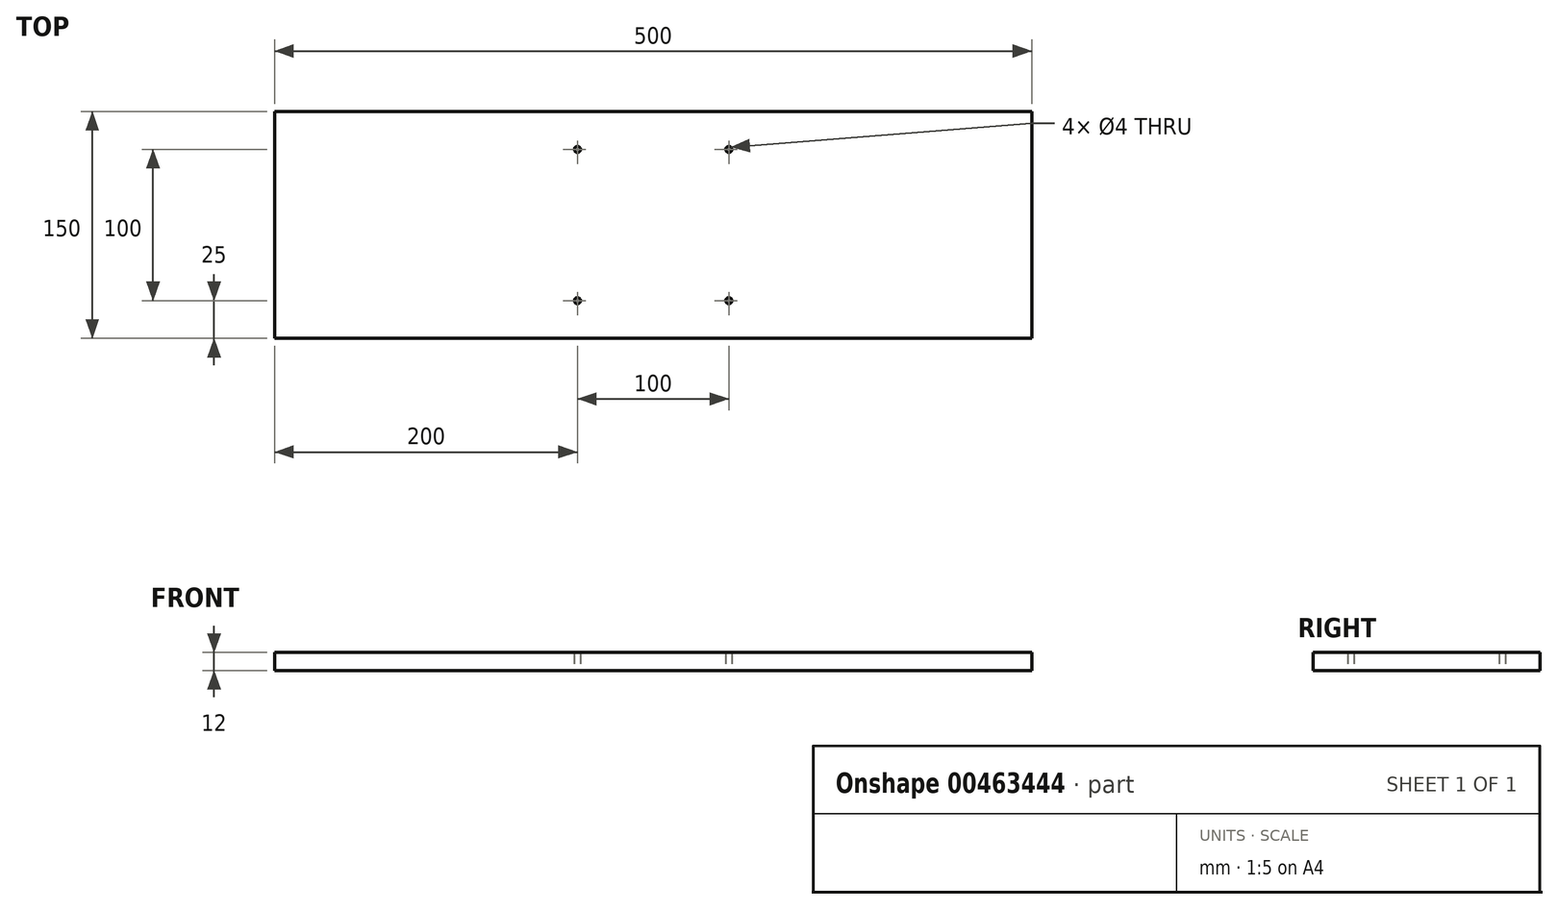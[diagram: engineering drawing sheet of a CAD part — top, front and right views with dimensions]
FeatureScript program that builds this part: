
annotation { "Feature Type Name" : "Feature", "Feature Type Description" : "" }
export const myFeature = defineFeature(function(context is Context, id is Id, definition is map)
    precondition{}
    {
        {
            var Q0;
            Q0=qCreatedBy(makeId("Top.planeOp"),FACE);
            var sketch = newSketch(context, id + "F0", { "sketchPlane" : qUnion([Q0])});
            skLineSegment(sketch, "E0.bottom", {"start": v(0, 150) * mm, "end": v(500, 150) * mm});
            skLineSegment(sketch, "E0.top", {"start": v(0, 0) * mm, "end": v(500, 0) * mm});
            skLineSegment(sketch, "E0.left", {"start": v(0, 150) * mm, "end": v(0, 0) * mm});
            skLineSegment(sketch, "E0.right", {"start": v(500, 150) * mm, "end": v(500, 0) * mm});
            skLineSegment(sketch, "E1", {"start": v(250, 150) * mm, "end": v(250, 0) * mm, "construction": true});
            skLineSegment(sketch, "E2", {"start": v(0, 75) * mm, "end": v(500, 75) * mm, "construction": true});
            skPoint(sketch, "E3", {"position": v(200, 125) * mm});
            skPoint(sketch, "E4.MirrorP", {"position": v(300, 125) * mm});
            skPoint(sketch, "E5.MirrorP", {"position": v(200, 25) * mm});
            skPoint(sketch, "E6.MirrorP", {"position": v(300, 25) * mm});
            skCircle(sketch, "E7", {"center": v(200, 125) * mm, "radius": 2 * mm});
            skCircle(sketch, "E8", {"center": v(300, 125) * mm, "radius": 2 * mm});
            skCircle(sketch, "E9", {"center": v(300, 25) * mm, "radius": 2 * mm});
            skCircle(sketch, "E10", {"center": v(200, 25) * mm, "radius": 2 * mm});
            skSolve(sketch);
        }
        {
            var Q0;
            Q0=makeQuery(id+"F0.imprint","IMPRINT",FACE,{"disambiguationData":[TD([[makeQuery(id+"F0.imprint","IMPRINT",EDGE,{"derivedFrom":sQuery(id+"F0.wireOp",EDGE,"E0.bottom")}),-1.0]])]});
            extrude(context, id + "F1", {"entities" : qUnion([Q0]), "depth" : 12 * mm});
        }
    });
